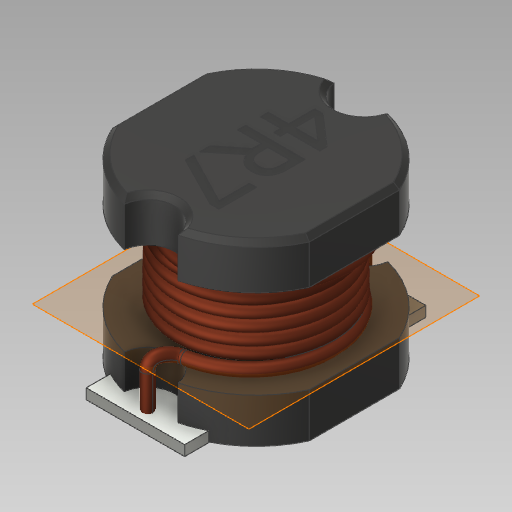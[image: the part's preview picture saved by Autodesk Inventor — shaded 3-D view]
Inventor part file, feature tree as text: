
AUTODESK INVENTOR PART (.ipt)
format: ipt  version: 2020 (Build 240168000, 168)  size: 728,064 bytes
history: native  units: in
note: dims shown in document units (in); Inventor stores cm internally (conversion verified against a paired STEP export)
features: sketch x11, projected_geometry x4, extrude x3, sweep x3, revolve x1, helix x1, plane x1, chamfer x1
ambient origin geometry x8: Origin, YZ Plane, XZ Plane, XY Plane, X Axis, Y Axis, Z Axis, Center Point
bodies: Solid1 (feature_tree), Solid2 (feature_tree)
feature tree (25):
  revolve  "Revolution1"  [1 undecoded]
  extrude  "Extrusion1"  Depth=0.18in
  helix  "Coil1"  [1 undecoded]
  sketch  "Sketch4"  dims[d7=1.0in d8=0.0in d9=0.012in]
  plane  "Work Plane1"
  sweep  "Sweep1"
  sweep  "Sweep2"
  sweep  "Sweep3"
  extrude  "Extrusion2"  TaperAngle=0.0deg  [1 undecoded]
  chamfer  "Chamfer1"  Distance=0.3937in
  extrude  "Extrusion3"  Depth=0.0025in
  sketch  "Sketch1"  dims[d0=0.22in d1=0.04in]
  sketch  "Sketch2"  dims[d2=0.09in d3=0.18in d4=90.0deg]
  sketch  "Sketch3"  dims[d5=0.055in d6=0.2in]
  sketch  "Sketch5"  dims[d10=0.09in d11=0.0121in]
  projected_geometry  "Projected Loop1"
  sketch  "Sketch6"  dims[d12=0.078in]
  projected_geometry  "Projected Loop2"
  sketch  "3D Sketch1"
  sketch  "Sketch7"  dims[d13=0.3937in d14=0.0in d15=90.0deg d16=90.0deg d17=0.0in d18=0.0in d19=0.0in d20=0.0in]
  projected_geometry  "Projected Loop3"
  sketch  "3D Sketch2"
  sketch  "Sketch8"  dims[d21=0.08in d22=0.3937in d23=0.3937in]
  projected_geometry  "Projected Loop4"
  sketch  "Sketch9"  dims[d24=0.0in d25=0.0in d26=0.0025in d28=0.3937in d29=0.3937in d30=0.0in d31=0.0in d32=0.025in d33=0.1in d34=0.01in d35=0.0005in d36=0.0in d37=0.0in d38=0.005in d39=0.125in d40=45.0deg d41=0.06in d42=0.0005in d43=0.0in]
note: 3 required parameter values undecoded (feature->parameter linkage not recoverable at this tier; creation-order binding heuristic only, values carry confidence <= 0.55)